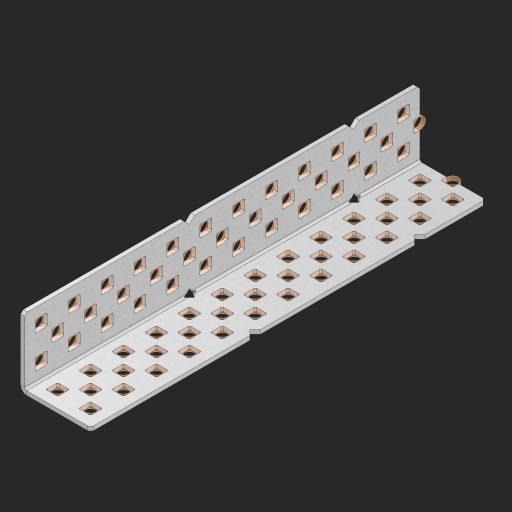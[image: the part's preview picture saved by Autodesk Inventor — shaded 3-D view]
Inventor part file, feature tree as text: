
AUTODESK INVENTOR PART (.ipt)
format: ipt  version: 2023 (Build 270158000, 158)  size: 1,121,792 bytes
history: native  units: in
note: dims shown in document units (in); Inventor stores cm internally (conversion verified against a paired STEP export)
features: other x78, extrude x70, sheet_metal_op x8, sketch x7, pattern_linear x2, mirror x1, chamfer x1
ambient origin geometry x8: Origin, YZ Plane, XZ Plane, XY Plane, X Axis, Y Axis, Z Axis, Center Point
bodies: Solid1 (feature_tree), Body (feature_tree)
feature tree (167):
  sheet_metal_op  "Flanges"
  sheet_metal_op  "Body Pattern"
  pattern_linear  "Center Pattern"  Spacing1=1.0in  [1 undecoded]
  other  "Arc Length"
  pattern_linear  "Notch Pattern"  Spacing1=0.25in  [1 undecoded]
  other  "Diagonal Plane"
  mirror  "Everything Mirrored"
  chamfer  "End Chamfer"
  sketch  "Sketch1"  dims[d0=1.0in]
  other  "Plate1"
  sketch  "Sketch2"  dims[d1=6.0in]
  other  "Plate2"
  sheet_metal_op  "Bend1"
  sheet_metal_op  "Corner1"
  sketch  "Sketch8"  dims[d2=0.0625in]
  sketch  "Sketch9"  dims[d3=0.0625in]
  other  "Srf91"
  sheet_metal_op  "Body Pattern Sketch"
  other  "Srf92"
  sketch  "Sketch13"  dims[d4=0.0312in]
  sketch  "Sketch15"  dims[d5=0.125in]
  sketch  "Sketch16"  dims[d6=0.0625in d7=1.0in d8=90.0deg d9=0.0312in d10=0.25in d11=0.0625in d12=0.0625in d49=0.182in d50=0.02in d52=0.25in d53=0.0625in d54=0.0in d55=0.172in d56=1.0in d57=0.0in d60=4.7244in d62=0.5in d63=0.7874in d65=0.5in d85=0.1473in d86=0.1782in d89=0.0625in d90=0.0in d91=0.04in d92=0.0491in d95=2.5in d96=0.04in d97=0.25in d98=45.0deg d99=0.25in d106=0.182in d107=0.02in d108=0.5in d110=0.0625in d111=0.0in d112=0.172in d113=0.5in d114=0.0in d117=0.5in d123=0.25in d125=0.25in d126=0.0491in d127=0.1473in d128=0.08in d129=0.04in d130=2.5in]
  other  "Srf786"
  other  "Srf856"
  other  "Srf857"
  other  "Srf858"
  other  "Srf859"
  other  "Srf860"
  other  "Srf861"
  other  "Srf889"
  other  "Srf890"
  other  "Srf891"
  other  "Srf1275"
  other  "Srf1276"
  other  "Srf1278"
  other  "Srf1279"
  other  "Srf1280"
  other  "Srf1281"
  other  "Srf1282"
  other  "Srf1283"
  other  "Srf1277"
  other  "Srf1285"
  other  "Srf1286"
  other  "Srf1287"
  other  "Srf1383"
  other  "Srf1384"
  other  "Srf1385"
  other  "Srf1386"
  other  "Srf1387"
  other  "Srf1388"
  other  "Srf1389"
  other  "Srf1390"
  other  "Srf1391"
  other  "Srf1392"
  other  "Srf1393"
  other  "Srf1394"
  other  "Srf1395"
  other  "Srf1396"
  other  "Srf1397"
  other  "Srf1398"
  other  "Srf1445"
  other  "Srf1446"
  other  "Srf1447"
  other  "Srf1448"
  other  "Srf1449"
  other  "Srf1450"
  other  "Srf1451"
  other  "Srf1452"
  other  "Srf1475"
  other  "Srf1476"
  other  "Srf1477"
  other  "Srf1478"
  other  "Srf1479"
  other  "Srf1480"
  other  "Srf1481"
  other  "Srf1482"
  other  "Srf1483"
  other  "Srf1484"
  other  "Srf1485"
  other  "Srf1486"
  other  "Srf1487"
  other  "Srf1488"
  other  "Srf1489"
  other  "Srf1490"
  other  "Srf1537"
  other  "Srf1538"
  other  "Srf1539"
  other  "Srf1540"
  other  "Srf1541"
  other  "Srf1542"
  other  "Srf1543"
  other  "Srf1544"
  sheet_metal_op  "Body Stamp"
  sheet_metal_op  "Body Circle"
  other  "Center Stamp"
  other  "Center Circle"
  sheet_metal_op  "Notch"
  extrude  "ExtrusionSrf92"  Depth=0.0625in
  extrude  "ExtrusionSrf856"  Depth=0.0625in
  extrude  "ExtrusionSrf857"  Depth=0.182in
  extrude  "ExtrusionSrf858"  Depth=0.02in
  extrude  "ExtrusionSrf859"  Depth=0.25in
  extrude  "ExtrusionSrf860"  Depth=0.0625in
  extrude  "ExtrusionSrf861"  TaperAngle=0.0deg  [1 undecoded]
  extrude  "ExtrusionSrf889"  Depth=2.5in
  extrude  "ExtrusionSrf890"  Depth=1.0in TaperAngle=0.0deg
  extrude  "ExtrusionSrf891"  Depth=2.5in
  extrude  "ExtrusionSrf1275"  Depth=0.5in
  extrude  "ExtrusionSrf1276"  Depth=2.5in
  extrude  "ExtrusionSrf1277"  Depth=2.5in
  extrude  "ExtrusionSrf1278"  Depth=0.0625in
  extrude  "ExtrusionSrf1279"  Depth=2.5in TaperAngle=0.0deg
  extrude  "ExtrusionSrf1280"  Depth=2.5in
  extrude  "ExtrusionSrf1281"  Depth=0.25in TaperAngle=45.0deg
  extrude  "ExtrusionSrf1282"  Depth=0.25in
  extrude  "ExtrusionSrf1345"  Depth=0.182in
  extrude  "ExtrusionSrf1346"  Depth=0.02in
  extrude  "ExtrusionSrf1347"  Depth=0.5in
  extrude  "ExtrusionSrf1348"  Depth=0.0625in
  extrude  "ExtrusionSrf1383"  TaperAngle=0.0deg  [1 undecoded]
  extrude  "ExtrusionSrf1384"  Depth=2.5in
  extrude  "ExtrusionSrf1385"  Depth=0.5in TaperAngle=0.0deg
  extrude  "ExtrusionSrf1386"  Depth=0.5in
  extrude  "ExtrusionSrf1387"  Depth=0.25in
  extrude  "ExtrusionSrf1388"  Depth=0.25in
  extrude  "ExtrusionSrf1389"  Depth=2.5in
  extrude  "ExtrusionSrf1390"  Depth=2.5in
  extrude  "ExtrusionSrf1391"  Depth=2.5in
  extrude  "ExtrusionSrf1392"  Depth=2.5in
  extrude  "ExtrusionSrf1393"  Depth=2.5in
  extrude  "ExtrusionSrf1394"  [1 undecoded]
  extrude  "ExtrusionSrf1395"  [1 undecoded]
  extrude  "ExtrusionSrf1396"  [1 undecoded]
  extrude  "ExtrusionSrf1397"  [1 undecoded]
  extrude  "ExtrusionSrf1398"  [1 undecoded]
  extrude  "ExtrusionSrf1445"  [1 undecoded]
  extrude  "ExtrusionSrf1446"  [1 undecoded]
  extrude  "ExtrusionSrf1447"  [1 undecoded]
  extrude  "ExtrusionSrf1448"  [1 undecoded]
  extrude  "ExtrusionSrf1449"  [1 undecoded]
  extrude  "ExtrusionSrf1450"  [1 undecoded]
  extrude  "ExtrusionSrf1451"  [1 undecoded]
  extrude  "ExtrusionSrf1452"  [1 undecoded]
  extrude  "ExtrusionSrf1475"  [1 undecoded]
  extrude  "ExtrusionSrf1476"  [1 undecoded]
  extrude  "ExtrusionSrf1477"  [1 undecoded]
  extrude  "ExtrusionSrf1478"  [1 undecoded]
  extrude  "ExtrusionSrf1479"  [1 undecoded]
  extrude  "ExtrusionSrf1480"  [1 undecoded]
  extrude  "ExtrusionSrf1481"  [1 undecoded]
  extrude  "ExtrusionSrf1482"  [1 undecoded]
  extrude  "ExtrusionSrf1483"  [1 undecoded]
  extrude  "ExtrusionSrf1484"  [1 undecoded]
  extrude  "ExtrusionSrf1485"  [1 undecoded]
  extrude  "ExtrusionSrf1486"  [1 undecoded]
  extrude  "ExtrusionSrf1487"  [1 undecoded]
  extrude  "ExtrusionSrf1488"  [1 undecoded]
  extrude  "ExtrusionSrf1489"  [1 undecoded]
  extrude  "ExtrusionSrf1490"  [1 undecoded]
  extrude  "ExtrusionSrf1537"  [1 undecoded]
  extrude  "ExtrusionSrf1538"  [1 undecoded]
  extrude  "ExtrusionSrf1539"  [1 undecoded]
  extrude  "ExtrusionSrf1540"  [1 undecoded]
  extrude  "ExtrusionSrf1541"  [1 undecoded]
  extrude  "ExtrusionSrf1542"  [1 undecoded]
  extrude  "ExtrusionSrf1543"  [1 undecoded]
  extrude  "ExtrusionSrf1544"  [1 undecoded]
note: 41 required parameter values undecoded (feature->parameter linkage not recoverable at this tier; creation-order binding heuristic only, values carry confidence <= 0.55)
